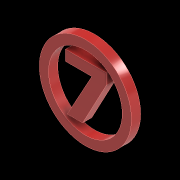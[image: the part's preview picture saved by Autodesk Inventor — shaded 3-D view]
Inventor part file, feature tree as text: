
AUTODESK INVENTOR PART (.ipt)
format: ipt  version: 2020 (Build 240168000, 168)  size: 136,704 bytes
history: native  units: mm
features: other x5, extrude x2, sketch x2
ambient origin geometry x8: Origin, YZ Plane, XZ Plane, XY Plane, X Axis, Y Axis, Z Axis, Center Point
bodies: Body1 (feature_tree)
feature tree (9):
  other  "自動販賣機.ipt"
  extrude  "擠出1"  Depth=10.0mm
  extrude  "擠出2"  Depth=10.0mm TaperAngle=0.0deg
  other  "實體49::自動販賣機.ipt"
  other  "標籤特徵1"
  sketch  "草圖1"
  sketch  "草圖2"
  other  "實體1"
  other  "投影切割邊1"
